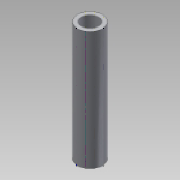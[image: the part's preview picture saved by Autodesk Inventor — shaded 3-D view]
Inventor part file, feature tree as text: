
AUTODESK INVENTOR PART (.ipt)
format: ipt  version: 2013 (Build 170138000, 138)  size: 87,552 bytes
history: native  units: mm
features: extrude x1, sketch x1
ambient origin geometry x8: Origin, YZ Plane, XZ Plane, XY Plane, X Axis, Y Axis, Z Axis, Center Point
bodies: Solid1 (feature_tree)
feature tree (2):
  extrude  "Extrusion1"  Depth=8.0mm
  sketch  "Sketch1"  dims[d0=5.3mm d3=8.0mm d4=38.1mm d5=0.0mm]
